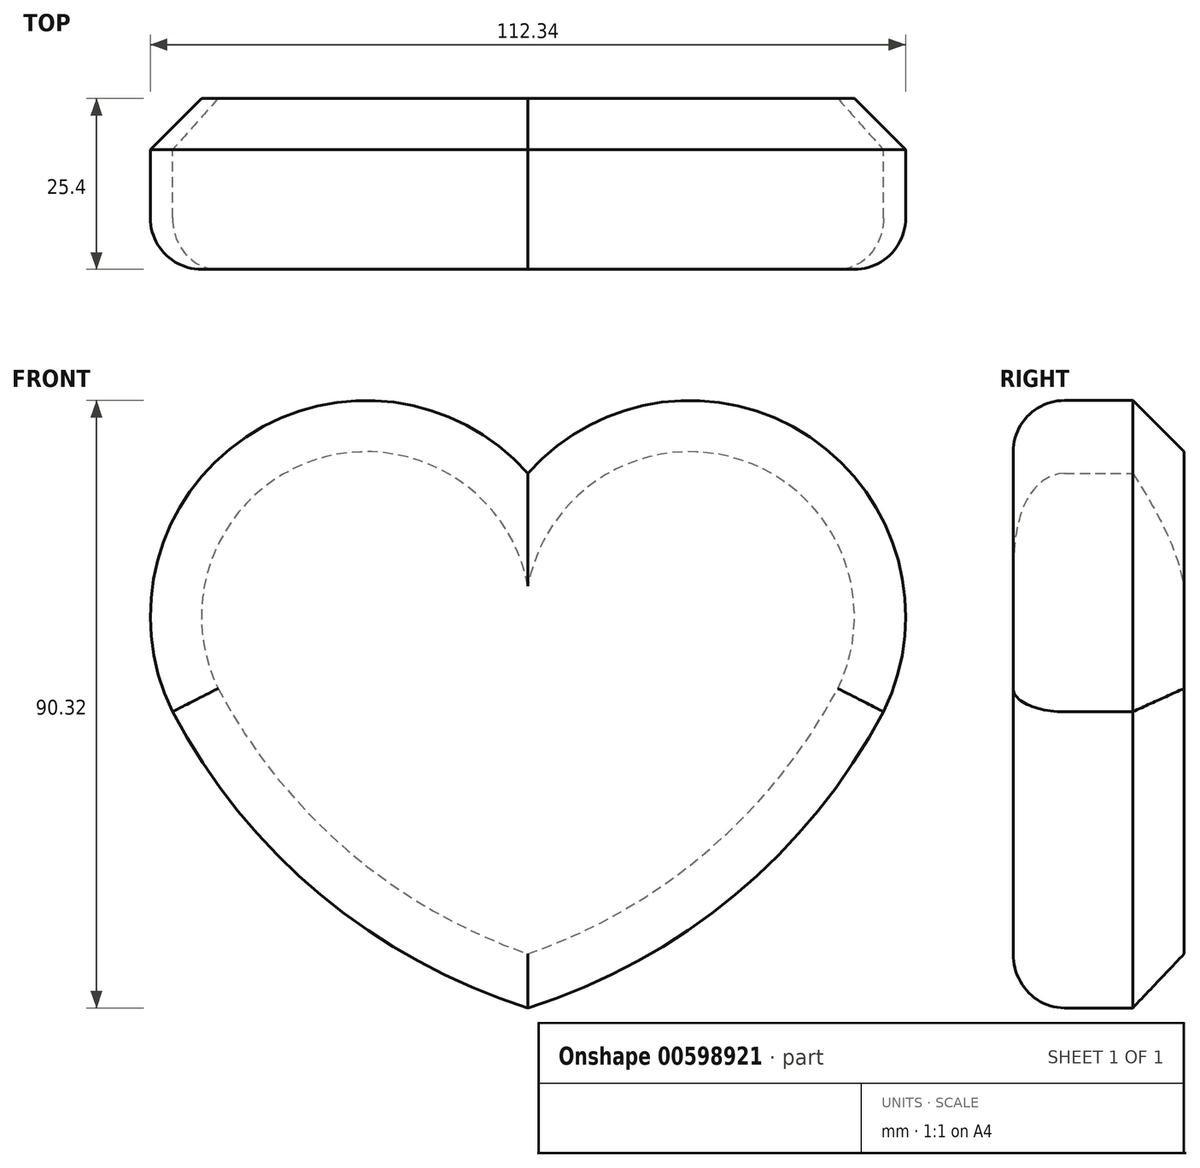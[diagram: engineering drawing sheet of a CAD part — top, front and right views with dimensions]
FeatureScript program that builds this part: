
annotation { "Feature Type Name" : "Feature", "Feature Type Description" : "" }
export const myFeature = defineFeature(function(context is Context, id is Id, definition is map)
    precondition{}
    {
        {
            var Q0;
            Q0=qCreatedBy(makeId("Front.planeOp"),FACE);
            var sketch = newSketch(context, id + "F0", { "sketchPlane" : qUnion([Q0])});
            skLineSegment(sketch, "E0", {"start": v(0, 0) * mm, "end": v(0, 58.21) * mm, "construction": true});
            skArc(sketch, "E1", {"start": v(0, 79.46) * mm, "mid": v(-43.1, 84.06) * mm, "end": v(-51.5, 41.53) * mm});
            skArc(sketch, "E2", {"start": v(-52.87, 44.04) * mm, "mid": v(-30.8, 16.8) * mm, "end": v(0, 0) * mm});
            skLineSegment(sketch, "E3", {"start": v(0, 0) * mm, "end": v(0, 79.46) * mm});
            skArc(sketch, "E4.MirrorCS", {"start": v(0, 79.46) * mm, "mid": v(43.1, 84.06) * mm, "end": v(51.5, 41.53) * mm});
            skArc(sketch, "E5.MirrorCS", {"start": v(52.87, 44.04) * mm, "mid": v(30.8, 16.8) * mm, "end": v(0, 0) * mm});
            skSolve(sketch);
        }
        {
            var Q0;
            {var subQ0=sQuery(id+"F0.wireOp",EDGE,"E3");Q0=makeQuery(id+"F0.imprint","IMPRINT",FACE,{"disambiguationData":[TD([[makeQuery(id+"F0.imprint","IMPRINT",EDGE,{"derivedFrom":subQ0}),-1.0]])]});}
            var Q1;
            {var subQ0=sQuery(id+"F0.wireOp",EDGE,"E3");Q1=makeQuery(id+"F0.imprint","IMPRINT",FACE,{"disambiguationData":[TD([[makeQuery(id+"F0.imprint","IMPRINT",EDGE,{"derivedFrom":subQ0}),1.0]])]});}
            extrude(context, id + "F1", {"entities" : qUnion([Q0, Q1]), "depth" : 25.4 * mm, "offsetDistance" : 25.4 * mm});
        }
        {
            var Q0;
            Q0=makeQuery(id+"F1.opExtrude","CAP_EDGE",EDGE,{"disambiguationData":[OSD([sQuery(id+"F0.wireOp",EDGE,"E1")])],"isStart":false});
            var Q1;
            Q1=makeQuery(id+"F1.opExtrude","CAP_FACE",FACE,{"disambiguationData":[OSD([sQuery(id+"F0.wireOp",EDGE,"E1"),sQuery(id+"F0.wireOp",EDGE,"E2"),sQuery(id+"F0.wireOp",EDGE,"E4.MirrorCS"),sQuery(id+"F0.wireOp",EDGE,"E5.MirrorCS")])],"isStart":false});
            fillet(context, id + "F2", {"entities" : qUnion([Q0, Q1]), "radius" : 7.62 * mm, "tangentPropagation" : true, "allowEdgeOverflow" : false});
        }
        {
            var Q0;
            Q0=makeQuery(id+"F1.opExtrude","CAP_EDGE",EDGE,{"disambiguationData":[OSD([sQuery(id+"F0.wireOp",EDGE,"E4.MirrorCS")])],"isStart":true});
            var Q1;
            Q1=makeQuery(id+"F1.opExtrude","CAP_EDGE",EDGE,{"disambiguationData":[OSD([sQuery(id+"F0.wireOp",EDGE,"E1")])],"isStart":true});
            var Q2;
            Q2=makeQuery(id+"F1.opExtrude","CAP_EDGE",EDGE,{"disambiguationData":[OSD([sQuery(id+"F0.wireOp",EDGE,"E2")])],"isStart":true});
            var Q3;
            Q3=makeQuery(id+"F1.opExtrude","CAP_EDGE",EDGE,{"disambiguationData":[OSD([sQuery(id+"F0.wireOp",EDGE,"E5.MirrorCS")])],"isStart":true});
            chamfer(context, id + "F3", {"entities" : qUnion([Q0, Q1, Q2, Q3]), "width" : 7.62 * mm, "tangentPropagation" : true});
        }
    });
